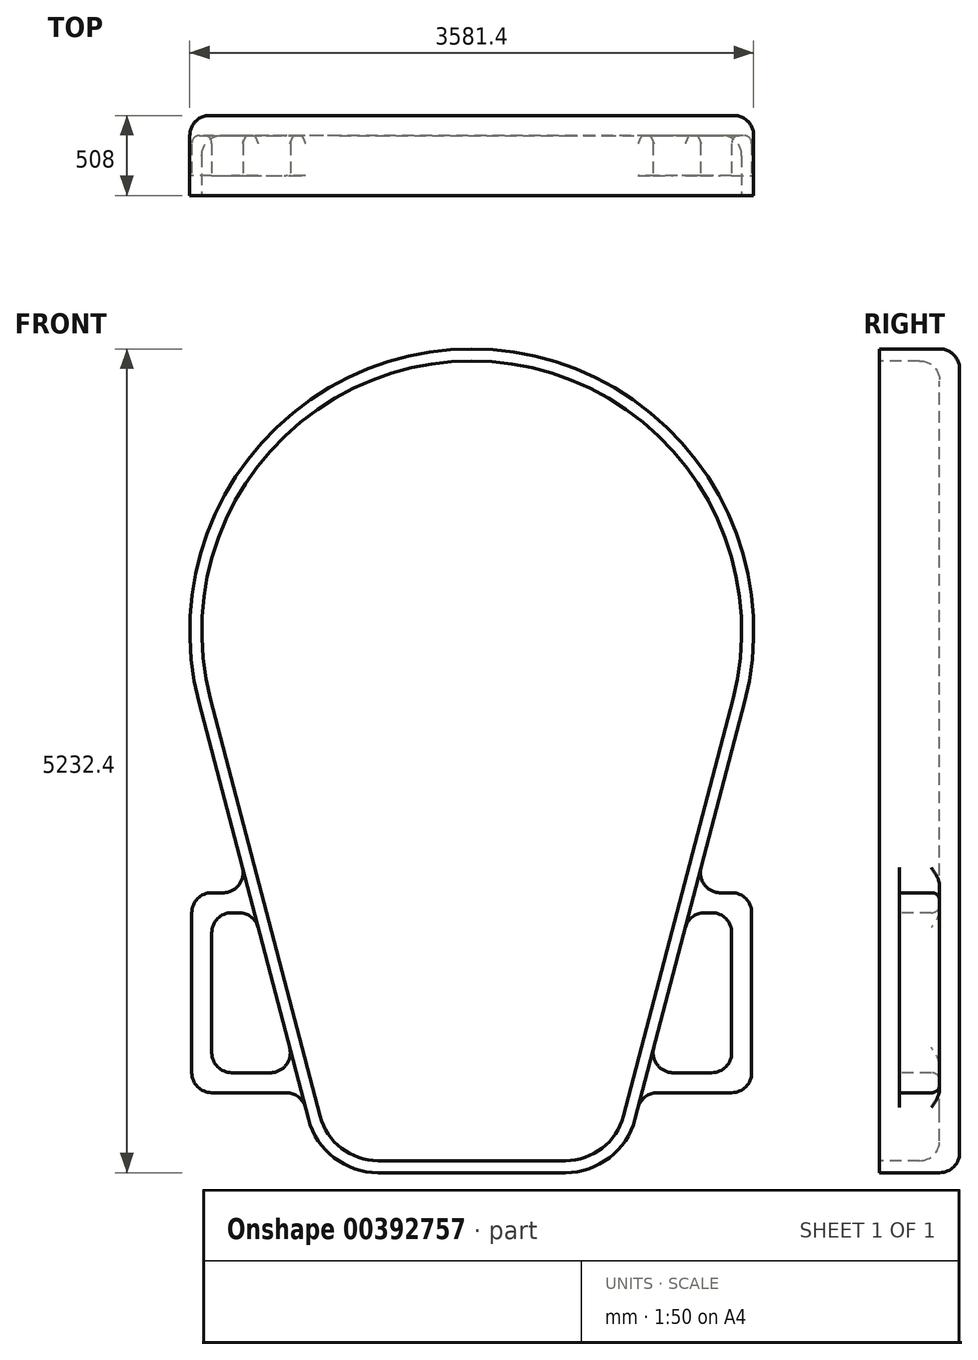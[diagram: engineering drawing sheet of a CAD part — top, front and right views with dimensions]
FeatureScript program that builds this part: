
annotation { "Feature Type Name" : "Feature", "Feature Type Description" : "" }
export const myFeature = defineFeature(function(context is Context, id is Id, definition is map)
    precondition{}
    {
        {
            var Q0;
            Q0=qCreatedBy(makeId("Front.planeOp"),FACE);
            var sketch = newSketch(context, id + "F0", { "sketchPlane" : qUnion([Q0])});
            skArc(sketch, "E0", {"start": v(1658.3, -435.38) * mm, "mid": v(0, 1714.5) * mm, "end": v(-1658.3, -435.38) * mm});
            skLineSegment(sketch, "E1", {"start": v(0, 0) * mm, "end": v(0, -3365.5) * mm, "construction": true});
            skLineSegment(sketch, "E2", {"start": v(-595.12, -3365.5) * mm, "end": v(595.12, -3365.5) * mm});
            skLineSegment(sketch, "E3", {"start": v(-963.63, -3081.25) * mm, "end": v(-1658.3, -435.38) * mm});
            skLineSegment(sketch, "E4", {"start": v(963.63, -3081.25) * mm, "end": v(1658.3, -435.38) * mm});
            skPoint(sketch, "E5.visualSharp", {"position": v(-889, -3365.5) * mm});
            skArc(sketch, "E5.filletArc", {"start": v(-963.63, -3081.25) * mm, "mid": v(-827.82, -3286.18) * mm, "end": v(-595.12, -3365.5) * mm});
            skPoint(sketch, "E6.visualSharp", {"position": v(889, -3365.5) * mm});
            skArc(sketch, "E6.filletArc", {"start": v(595.12, -3365.5) * mm, "mid": v(827.82, -3286.18) * mm, "end": v(963.63, -3081.25) * mm});
            skArc(sketch, "E7", {"start": v(1732, -454.73) * mm, "mid": v(0, 1790.7) * mm, "end": v(-1732, -454.73) * mm});
            skLineSegment(sketch, "E8", {"start": v(-595.12, -3441.7) * mm, "end": v(595.12, -3441.7) * mm});
            skLineSegment(sketch, "E9", {"start": v(-1732, -454.73) * mm, "end": v(-1037.33, -3100.6) * mm});
            skLineSegment(sketch, "E10", {"start": v(1732, -454.73) * mm, "end": v(1456.4, -1504.45) * mm});
            skArc(sketch, "E11.filletArc", {"start": v(-1037.33, -3100.6) * mm, "mid": v(-874.36, -3346.52) * mm, "end": v(-595.12, -3441.7) * mm});
            skArc(sketch, "E12.filletArc", {"start": v(595.12, -3441.7) * mm, "mid": v(874.36, -3346.52) * mm, "end": v(1037.33, -3100.6) * mm});
            skLineSegment(sketch, "E13", {"start": v(1778, -1790.7) * mm, "end": v(1778, -2806.7) * mm});
            skLineSegment(sketch, "E14", {"start": v(1651, -1663.7) * mm, "end": v(1579.24, -1663.7) * mm});
            skLineSegment(sketch, "E15", {"start": v(1651, -2933.7) * mm, "end": v(1179.11, -2933.7) * mm});
            skArc(sketch, "E16.filletArc", {"start": v(1456.4, -1504.45) * mm, "mid": v(1478.67, -1614.27) * mm, "end": v(1579.24, -1663.7) * mm});
            skPoint(sketch, "E17.visualSharp", {"position": v(1778, -1663.7) * mm});
            skArc(sketch, "E17.filletArc", {"start": v(1778, -1790.7) * mm, "mid": v(1740.8, -1700.9) * mm, "end": v(1651, -1663.7) * mm});
            skPoint(sketch, "E18.visualSharp", {"position": v(1778, -2933.7) * mm});
            skArc(sketch, "E18.filletArc", {"start": v(1651, -2933.7) * mm, "mid": v(1740.8, -2896.5) * mm, "end": v(1778, -2806.7) * mm});
            skLineSegment(sketch, "E19", {"start": v(1037.33, -3100.6) * mm, "end": v(1056.27, -3028.45) * mm});
            skPoint(sketch, "E20.visualSharp", {"position": v(1081.15, -2933.7) * mm});
            skArc(sketch, "E20.filletArc", {"start": v(1179.11, -2933.7) * mm, "mid": v(1101.54, -2960.14) * mm, "end": v(1056.27, -3028.45) * mm});
            skLineSegment(sketch, "E21", {"start": v(1356.37, -1885.45) * mm, "end": v(1156.3, -2647.45) * mm});
            skLineSegment(sketch, "E22", {"start": v(1651, -1917.7) * mm, "end": v(1651, -2679.7) * mm});
            skLineSegment(sketch, "E23", {"start": v(1479.2, -1790.7) * mm, "end": v(1524, -1790.7) * mm});
            skLineSegment(sketch, "E24", {"start": v(1524, -2806.7) * mm, "end": v(1279.14, -2806.7) * mm});
            skPoint(sketch, "E25.visualSharp", {"position": v(1381.24, -1790.7) * mm});
            skArc(sketch, "E25.filletArc", {"start": v(1479.2, -1790.7) * mm, "mid": v(1401.64, -1817.14) * mm, "end": v(1356.37, -1885.45) * mm});
            skArc(sketch, "E26.filletArc", {"start": v(1651, -1917.7) * mm, "mid": v(1613.8, -1827.9) * mm, "end": v(1524, -1790.7) * mm});
            skArc(sketch, "E27.filletArc", {"start": v(1524, -2806.7) * mm, "mid": v(1613.8, -2769.5) * mm, "end": v(1651, -2679.7) * mm});
            skPoint(sketch, "E28.visualSharp", {"position": v(1114.5, -2806.7) * mm});
            skArc(sketch, "E28.filletArc", {"start": v(1156.3, -2647.45) * mm, "mid": v(1178.58, -2757.27) * mm, "end": v(1279.14, -2806.7) * mm});
            skLineSegment(sketch, "E29.MirrorCS", {"start": v(-1479.2, -1790.7) * mm, "end": v(-1524, -1790.7) * mm});
            skArc(sketch, "E30.MirrorCS", {"start": v(-1651, -1917.7) * mm, "mid": v(-1613.8, -1827.9) * mm, "end": v(-1524, -1790.7) * mm});
            skArc(sketch, "E31.MirrorCS", {"start": v(-1479.2, -1790.7) * mm, "mid": v(-1401.64, -1817.14) * mm, "end": v(-1356.37, -1885.45) * mm});
            skLineSegment(sketch, "E32.MirrorCS", {"start": v(-1356.37, -1885.45) * mm, "end": v(-1156.3, -2647.45) * mm});
            skLineSegment(sketch, "E33.MirrorCS", {"start": v(-1651, -1917.7) * mm, "end": v(-1651, -2679.7) * mm});
            skArc(sketch, "E34.MirrorCS", {"start": v(-1524, -2806.7) * mm, "mid": v(-1613.8, -2769.5) * mm, "end": v(-1651, -2679.7) * mm});
            skLineSegment(sketch, "E35.MirrorCS", {"start": v(-1524, -2806.7) * mm, "end": v(-1279.14, -2806.7) * mm});
            skArc(sketch, "E36.MirrorCS", {"start": v(-1156.3, -2647.45) * mm, "mid": v(-1178.58, -2757.27) * mm, "end": v(-1279.14, -2806.7) * mm});
            skArc(sketch, "E37.MirrorCS", {"start": v(-1179.11, -2933.7) * mm, "mid": v(-1101.54, -2960.14) * mm, "end": v(-1056.27, -3028.45) * mm});
            skLineSegment(sketch, "E38.MirrorCS", {"start": v(-1651, -2933.7) * mm, "end": v(-1179.11, -2933.7) * mm});
            skArc(sketch, "E39.MirrorCS", {"start": v(-1651, -2933.7) * mm, "mid": v(-1740.8, -2896.5) * mm, "end": v(-1778, -2806.7) * mm});
            skLineSegment(sketch, "E40.MirrorCS", {"start": v(-1651, -1663.7) * mm, "end": v(-1579.24, -1663.7) * mm});
            skLineSegment(sketch, "E41.MirrorCS", {"start": v(-1778, -1790.7) * mm, "end": v(-1778, -2806.7) * mm});
            skArc(sketch, "E42.MirrorCS", {"start": v(-1778, -1790.7) * mm, "mid": v(-1740.8, -1700.9) * mm, "end": v(-1651, -1663.7) * mm});
            skArc(sketch, "E43.MirrorCS", {"start": v(-1456.4, -1504.45) * mm, "mid": v(-1478.67, -1614.27) * mm, "end": v(-1579.24, -1663.7) * mm});
            skLineSegment(sketch, "E44", {"start": v(1356.37, -1885.45) * mm, "end": v(1456.4, -1504.45) * mm});
            skLineSegment(sketch, "E45", {"start": v(1056.27, -3028.45) * mm, "end": v(1156.3, -2647.45) * mm});
            skSolve(sketch);
        }
        {
            var Q0;
            Q0=makeQuery(id+"F0.imprint","IMPRINT",FACE,{"disambiguationData":[TD([[makeQuery(id+"F0.imprint","IMPRINT",EDGE,{"derivedFrom":sQuery(id+"F0.wireOp",EDGE,"E0")}),-1.0]])]});
            var Q1;
            Q1=makeQuery(id+"F0.imprint","IMPRINT",FACE,{"disambiguationData":[TD([[makeQuery(id+"F0.imprint","IMPRINT",EDGE,{"derivedFrom":sQuery(id+"F0.wireOp",EDGE,"E0")}),1.0]])]});
            extrude(context, id + "F1", {"entities" : qUnion([Q0, Q1]), "oppositeDirection" : true, "depth" : 508 * mm});
        }
        {
            var Q0;
            Q0=makeQuery(id+"F0.imprint","IMPRINT",FACE,{"disambiguationData":[TD([[makeQuery(id+"F0.imprint","IMPRINT",EDGE,{"derivedFrom":sQuery(id+"F0.wireOp",EDGE,"E0")}),1.0]])]});
            extrude(context, id + "F2", {"entities" : qUnion([Q0]), "operationType" : NewBodyOperationType.REMOVE, "oppositeDirection" : true, "depth" : 381 * mm});
        }
        {
            var Q0;
            Q0=makeQuery(id+"F0.imprint","IMPRINT",FACE,{"disambiguationData":[TD([[makeQuery(id+"F0.imprint","IMPRINT",EDGE,{"derivedFrom":sQuery(id+"F0.wireOp",EDGE,"E29.MirrorCS")}),-1.0]])]});
            var Q1;
            Q1=makeQuery(id+"F0.imprint","IMPRINT",FACE,{"disambiguationData":[TD([[makeQuery(id+"F0.imprint","IMPRINT",EDGE,{"derivedFrom":sQuery(id+"F0.wireOp",EDGE,"E13")}),-1.0]])]});
            extrude(context, id + "F3", {"entities" : qUnion([Q0, Q1]), "operationType" : NewBodyOperationType.ADD, "oppositeDirection" : true, "depth" : 381 * mm});
        }
        {
            var Q0;
            Q0=makeQuery(id+"F0.imprint","IMPRINT",FACE,{"disambiguationData":[TD([[makeQuery(id+"F0.imprint","IMPRINT",EDGE,{"derivedFrom":sQuery(id+"F0.wireOp",EDGE,"E29.MirrorCS")}),-1.0]])]});
            var Q1;
            Q1=makeQuery(id+"F0.imprint","IMPRINT",FACE,{"disambiguationData":[TD([[makeQuery(id+"F0.imprint","IMPRINT",EDGE,{"derivedFrom":sQuery(id+"F0.wireOp",EDGE,"E13")}),-1.0]])]});
            extrude(context, id + "F4", {"entities" : qUnion([Q0, Q1]), "operationType" : NewBodyOperationType.REMOVE, "oppositeDirection" : true, "depth" : 127 * mm});
        }
        {
            var Q0;
            Q0=makeQuery(id+"F4.boolean.opBoolean","COPY",EDGE,{"derivedFrom":makeQuery(id+"F4.opExtrude","CAP_EDGE",EDGE,{"disambiguationData":[OSD([sQuery(id+"F0.wireOp",EDGE,"E43.MirrorCS")])],"isStart":false})});
            var Q1;
            Q1=makeQuery(id+"F4.boolean.opBoolean","COPY",EDGE,{"derivedFrom":makeQuery(id+"F4.opExtrude","CAP_EDGE",EDGE,{"disambiguationData":[OSD([sQuery(id+"F0.wireOp",EDGE,"E31.MirrorCS")])],"isStart":false})});
            var Q2;
            Q2=makeQuery(id+"F4.boolean.opBoolean","COPY",EDGE,{"derivedFrom":makeQuery(id+"F4.opExtrude","CAP_EDGE",EDGE,{"disambiguationData":[OSD([sQuery(id+"F0.wireOp",EDGE,"E27.filletArc")])],"isStart":false})});
            var Q3;
            Q3=makeQuery(id+"F4.boolean.opBoolean","COPY",EDGE,{"derivedFrom":makeQuery(id+"F4.opExtrude","CAP_EDGE",EDGE,{"disambiguationData":[OSD([sQuery(id+"F0.wireOp",EDGE,"E18.filletArc")])],"isStart":false})});
            var Q4;
            Q4=makeQuery(id+"F3.opExtrude","CAP_EDGE",EDGE,{"disambiguationData":[OSD([sQuery(id+"F0.wireOp",EDGE,"E36.MirrorCS")])],"isStart":false});
            var Q5;
            Q5=makeQuery(id+"F3.opExtrude","CAP_EDGE",EDGE,{"disambiguationData":[OSD([sQuery(id+"F0.wireOp",EDGE,"E37.MirrorCS")])],"isStart":false});
            var Q6;
            Q6=makeQuery(id+"F3.opExtrude","CAP_EDGE",EDGE,{"disambiguationData":[OSD([sQuery(id+"F0.wireOp",EDGE,"E20.filletArc")])],"isStart":false});
            var Q7;
            Q7=makeQuery(id+"F3.opExtrude","CAP_EDGE",EDGE,{"disambiguationData":[OSD([sQuery(id+"F0.wireOp",EDGE,"E28.filletArc")])],"isStart":false});
            fillet(context, id + "F5", {"entities" : qUnion([Q0, Q1, Q2, Q3, Q4, Q5, Q6, Q7]), "radius" : 50.8 * mm, "tangentPropagation" : true, "allowEdgeOverflow" : false});
        }
        {
            var Q0;
            Q0=makeQuery(id+"F1.opExtrude","CAP_EDGE",EDGE,{"disambiguationData":[OSD([sQuery(id+"F0.wireOp",EDGE,"E11.filletArc")])],"isStart":false});
            var Q1;
            Q1=makeQuery(id+"F2.boolean.opBoolean","COPY",EDGE,{"derivedFrom":makeQuery(id+"F2.opExtrude","CAP_EDGE",EDGE,{"disambiguationData":[OSD([sQuery(id+"F0.wireOp",EDGE,"E0")])],"isStart":false})});
            fillet(context, id + "F6", {"entities" : qUnion([Q0, Q1]), "radius" : 127 * mm, "tangentPropagation" : true, "allowEdgeOverflow" : false});
        }
    });
